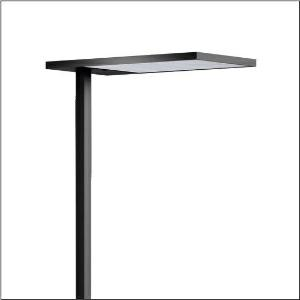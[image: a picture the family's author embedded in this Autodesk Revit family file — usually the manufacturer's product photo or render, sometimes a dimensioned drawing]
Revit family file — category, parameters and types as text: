
# Revit family: silica_r__21_floor_r_51mx53sg4db_4ec3
name_source: partatom
category: Lighting Fixtures
units: mm (PartAtom-declared; Revit-internal decimal feet)

## family parameters
Cut with Voids When Loaded = No
Host = Face
Light Source = No
Part Type = Normal
Room Calculation Point = No
Round Connector Dimension = Use Diameter
Shared = No

## types (1)
- Silica® 21 Floor R (1 x LED, 15000 lm, 106.4 W, 4000K)
    Apparent Load = 106 VA
    CIE Flux Codes = 54 86 97 13 100
    Color Rendering = 80
    Color Temperature = 4000K
    Default Elevation = 1800 mm
    Description = Silica® 21 Floor R, floorstanding luminaire, of PMMA, primary optical cover: prismatic diffuser, of PMMA, CAT 2 (L<= 3000cd/m²), light emission: indirect/direct distribution, primary light characteristic: symmetric, installation type: not mounted, LED, rated luminous flux: 15.000lm, luminous efficacy: 141lm/W, light colour: 840, colour temperature: 4000K, daylight-dependent control, mains connection: 230V, 50Hz, connection cable pre-assembled, cable length: 2,5m, rated input power: 106.4W, luminaire head, of aluminium, jet black (RAL 9005), length: 650mm, width: 350mm, supporting column, angular, of aluminium, jet black (RAL 9005), baseplate, of steel, jet black (RAL 9005), protection rating (complete): IP20, insulation class (complete): insulation class I (protective earthing), certification: CE, standard: EN 50419, packaging unit: 1 piece
    Height = 18 mm
    Lamp = 1 x LED
    Lamp Light Flux = 15000 lm
    Lamp Power = 106.4 W
    Lamp count = 1
    Length = 650 mm
    Luminous efficacy = 141 lm/W
    Manufacturer = Siteco
    ModVariant = No
    Model = 51MX53SG4DB
    Mounting Place = Floor
    Mounting Type = Freestanding
    Number of Poles = 1
    OnlyDefault = Yes
    Power Factor = 1
    Product Name = Silica® 21 Floor R
    Product group = floorstanding luminaire
    ProductGroupID = 1301
    Protection Class = Protection class I
    Protection Degree = IP 20
    RLX_Detail_Level = 1
    RLX_Emergency_Light_Flux = 0 lm
    RLX_Emergency_Type = 0
    RLX_Emergency_Type_DB = No
    RlxData = <blob elided: 21997 chars, md5=59a1f143>
    Socket = socket
    Standby Power = 0 W
    System Light Flux = 15000 lm
    System Power = 106 W
    Type Comments = Product without accessories
    Type Image = l_1007011.jpg
    URL = http://relux.com
    VarID = ---
    Voltage = 0 V
    Weight = 0.00 kg
    Width = 350 mm

## geometry (parser evidence)
native form markers: Blend x4, Sweep x13
no freeform markers — native parametric forms only
